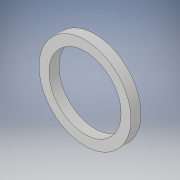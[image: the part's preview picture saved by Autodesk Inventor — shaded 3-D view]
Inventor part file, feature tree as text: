
AUTODESK INVENTOR PART (.ipt)
format: ipt  version: 2019 (Build 230136000, 136)  size: 103,936 bytes
history: native  units: mm
features: extrude x2, sketch x2
ambient origin geometry x8: Origin, YZ Plane, XZ Plane, XY Plane, X Axis, Y Axis, Z Axis, Center Point
bodies: Solid1 (feature_tree)
feature tree (4):
  extrude  "Extrusion1"  Depth=4.0mm TaperAngle=0.0deg
  extrude  "Extrusion2"  Depth=4.0mm TaperAngle=0.0deg
  sketch  "Sketch1"  dims[d0=37.0mm d1=4.0mm d2=0.0mm]
  sketch  "Sketch3"  dims[d3=29.0mm d4=4.0mm d5=0.0mm]
